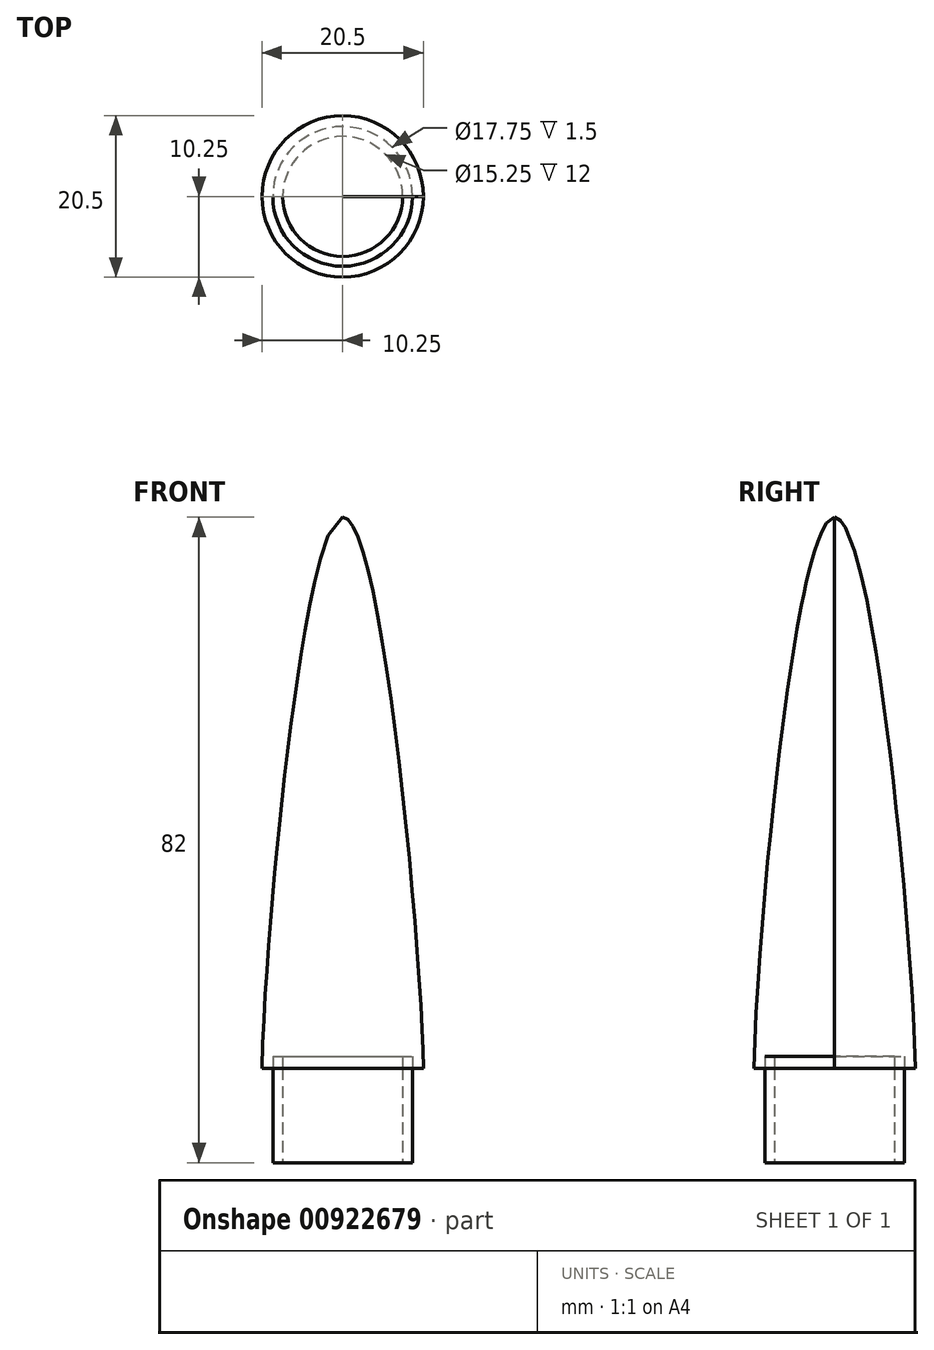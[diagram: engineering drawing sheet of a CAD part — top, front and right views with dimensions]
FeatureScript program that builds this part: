
annotation { "Feature Type Name" : "Feature", "Feature Type Description" : "" }
export const myFeature = defineFeature(function(context is Context, id is Id, definition is map)
    precondition{}
    {
        {
            var Q0;
            Q0=qCreatedBy(makeId("Front.planeOp"),FACE);
            var sketch = newSketch(context, id + "F0", { "sketchPlane" : qUnion([Q0])});
            skLineSegment(sketch, "E0", {"start": v(0, 0) * mm, "end": v(0, 70) * mm});
            skFitSpline(sketch, "E1", {"points": [v(0, 70) * mm, v(10.25, 0) * mm], "startDerivative": vector(15, 0) * mm, "endDerivative": vector(0.75, -48) * mm});
            skFitSpline(sketch, "E2.0", {"points": [v(-0.5, 68.7) * mm, v(-0.49, 68.7) * mm, v(-0.46, 68.67) * mm, v(-0.42, 68.64) * mm, v(-0.4, 68.62) * mm, v(-0.38, 68.61) * mm, v(-0.37, 68.6) * mm, v(-0.37, 68.6) * mm, v(-0.36, 68.6) * mm, v(-0.36, 68.6) * mm, v(-0.36, 68.6) * mm, v(-0.36, 68.6) * mm, v(-0.36, 68.6) * mm, v(-0.36, 68.6) * mm, v(-0.35, 68.58) * mm, v(-0.32, 68.56) * mm, v(-0.28, 68.52) * mm, v(-0.22, 68.44) * mm, v(-0.13, 68.3) * mm, v(0.01, 68.08) * mm, v(0.2, 67.72) * mm, v(0.46, 67.15) * mm, v(0.8, 66.25) * mm, v(1.23, 64.93) * mm, v(1.65, 63.38) * mm, v(2.08, 61.62) * mm, v(2.64, 59.04) * mm, v(3.33, 55.39) * mm, v(4.12, 50.47) * mm, v(4.87, 45.16) * mm, v(5.58, 39.56) * mm, v(6.24, 33.82) * mm, v(7.03, 26.12) * mm, v(7.85, 16.74) * mm, v(8.52, 6.87) * mm, v(8.72, 1.89) * mm, v(8.75, -0.02) * mm]});
            skLineSegment(sketch, "E3", {"start": v(0, 0) * mm, "end": v(10.25, 0) * mm});
            skLineSegment(sketch, "E4.bottom", {"start": v(7.62, 1.5) * mm, "end": v(8.88, 1.5) * mm});
            skLineSegment(sketch, "E4.top", {"start": v(7.63, -12) * mm, "end": v(8.88, -12) * mm});
            skLineSegment(sketch, "E4.left", {"start": v(7.62, 1.5) * mm, "end": v(7.62, -12) * mm});
            skLineSegment(sketch, "E4.right", {"start": v(8.88, 1.5) * mm, "end": v(8.88, -12) * mm});
            skSolve(sketch);
        }
        {
            var Q0;
            {var subQ1=sQuery(id+"F0.wireOp",EDGE,"E1");Q0=makeQuery(id+"F0.imprint","IMPRINT",FACE,{"disambiguationData":[TD([[makeQuery(id+"F0.imprint","IMPRINT",EDGE,{"derivedFrom":subQ1}),-1.0]])]});}
            var Q1;
            {var subQ1=sQuery(id+"F0.wireOp",EDGE,"E4.top");Q1=makeQuery(id+"F0.imprint","IMPRINT",FACE,{"disambiguationData":[TD([[makeQuery(id+"F0.imprint","IMPRINT",EDGE,{"derivedFrom":subQ1}),1.0]])]});}
            var Q2;
            {var subQ0=sQuery(id+"F0.wireOp",EDGE,"E3");var subQ1=sQuery(id+"F0.wireOp",EDGE,"E2.0");var subQ2=makeQuery(id+"F0.imprint","INTERSECT",VERTEX,{"derivedFrom":[subQ1,subQ0]});Q2=makeQuery(id+"F0.imprint","IMPRINT",FACE,{"disambiguationData":[TD([[makeQuery(id+"F0.imprint","IMPRINT",EDGE,{"disambiguationData":[TD([[subQ2,1.0]])],"derivedFrom":subQ1}),-1.0]])]});}
            var Q3;
            {var subQ0=sQuery(id+"F0.wireOp",EDGE,"E3");var subQ1=sQuery(id+"F0.wireOp",EDGE,"E2.0");var subQ2=makeQuery(id+"F0.imprint","INTERSECT",VERTEX,{"derivedFrom":[subQ1,subQ0]});Q3=makeQuery(id+"F0.imprint","IMPRINT",FACE,{"disambiguationData":[TD([[makeQuery(id+"F0.imprint","IMPRINT",EDGE,{"disambiguationData":[TD([[subQ2,1.0]])],"derivedFrom":subQ1}),1.0]])]});}
            var Q4;
            Q4=sQuery(id+"F0.wireOp",EDGE,"E0");
            revolve(context, id + "F1", {"surfaceOperationType" : NewSurfaceOperationType.NEW, "entities" : qUnion([Q0, Q1, Q2, Q3]), "axis" : qUnion([Q4]), "revolveType" : RevolveType.FULL});
        }
    });
